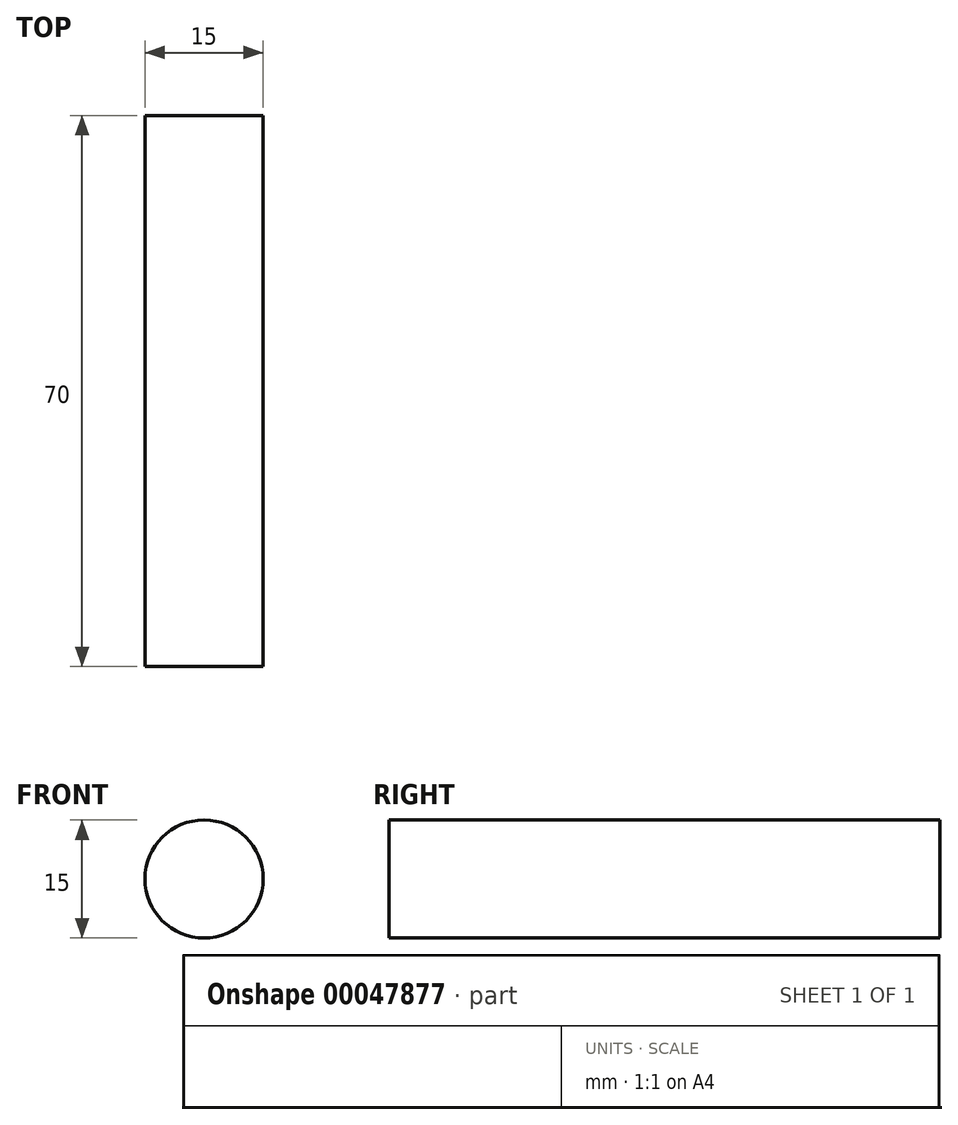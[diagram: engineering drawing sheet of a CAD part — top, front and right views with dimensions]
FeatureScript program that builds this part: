
annotation { "Feature Type Name" : "Feature", "Feature Type Description" : "" }
export const myFeature = defineFeature(function(context is Context, id is Id, definition is map)
    precondition{}
    {
        {
            var Q0;
            Q0=qCreatedBy(makeId("Front.planeOp"),FACE);
            var sketch = newSketch(context, id + "F0", { "sketchPlane" : qUnion([Q0])});
            skCircle(sketch, "E0", {"center": v(0, 0) * mm, "radius": 7.5 * mm});
            skSolve(sketch);
        }
        {
            var Q0;
            Q0=makeQuery(id+"F0.imprint","IMPRINT",FACE,{"disambiguationData":[TD([[makeQuery(id+"F0.imprint","IMPRINT",EDGE,{"derivedFrom":sQuery(id+"F0.wireOp",EDGE,"E0")}),1.0]])]});
            extrude(context, id + "F1", {"entities" : qUnion([Q0]), "depth" : 70 * mm});
        }
    });
